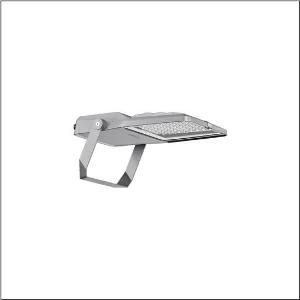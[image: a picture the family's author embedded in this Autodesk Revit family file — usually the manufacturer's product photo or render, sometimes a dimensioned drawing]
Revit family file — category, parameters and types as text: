
# Revit family: floodlight_fl_21_mini___pl64_5xa7776c2e1a_42f0
name_source: partatom
category: Lighting Fixtures
units: mm (PartAtom-declared; Revit-internal decimal feet)

## family parameters
Cut with Voids When Loaded = No
Host = Face
Light Source = No
Part Type = Normal
Room Calculation Point = No
Round Connector Dimension = Use Diameter
Shared = No

## types (1)
- --- (1 x LED, 11770 lm, 89 W, 3000K)
    Apparent Load = 89 VA
    CIE Flux Codes = 28 80 98 100 100
    Color Rendering = 70
    Color Temperature = 3000K
    Default Elevation = 1800 mm
    Description = Floodlight FL 21 mini, floodlight, primary light control with lens, of PMMA, primary optical cover: protective disc, of toughened safety glass, transparent, light distribution: PL64, light emission: direct distribution, installation type: surface-mounted, LED, High Power LED, rated luminous flux: 11.770lm, luminous efficacy: 132lm/W, light colour: 730, colour temperature: 3000K, control gear: Smart Interface (Zhaga), control: flexible luminous flux parameterisation, time-dependent luminous flux control, constant luminous flux control, overheat protection, pre-setting: logarithmic dimming characteristic, with terminal, 6-pole, mains connection: 220..240V, AC, 50/60Hz, start of lifetime: 89W, end of service life: 94W, reduction: 43W, luminaire housing, of diecast aluminium, powder-coated, SITECO metallic grey (DB 702S), corrosivity category C5 mid according to DIN EN ISO 12944, suitable for swimming pools, chlorine-resistant, sealing non-destructively replaceable, mounting bracket, of steel, galvanised, powder-coated, SITECO metallic grey (DB 702S), Smart Interface below and above, protection rating (complete): IP66, insulation class (complete): insulation class II (safety insulation), certification: CE, ENEC, VDE, protection symbol: D, impact resistance: IK08, permissible operating ambient temperature: -40..+40°C, permissible operating ambient temperature for outdoor applications: -40..+50°C, standard: DIN EN 12944, LABS conformity tested according to VDMA 24364:2018-05, packaging unit: 1 piece

Light Distribution: PL64
    Height = 70 mm
    Lamp = 1 x LED
    Lamp Light Flux = 11770 lm
    Lamp Power = 89 W
    Lamp count = 1
    Length = 485 mm
    Luminous efficacy = 132 lm/W
    Manufacturer = Siteco
    ModVariant = No
    Model = 5XA7776C2E1A
    Mounting Place = Pole
    Mounting Type = Pole annexe
    Number of Poles = 1
    OnlyDefault = Yes
    Power Factor = 1
    Product Name = Floodlight FL 21 mini | PL64
    Product group = floodlight | pylon annexe
    ProductGroupID = 6201
    Protection Class = Protection class II
    Protection Degree = IP 66
    RLX_Detail_Level = 1
    RLX_Emergency_Light_Flux = 0 lm
    RLX_Emergency_Type = 0
    RLX_Emergency_Type_DB = No
    RlxData = <blob elided: 95997 chars, md5=2740ca23>
    Socket = socket
    Standby Power = 0 W
    System Light Flux = 11770 lm
    System Power = 89 W
    Type Comments = factory setting: luminous flux: 100 % | dim-lin: 254 | 456 mA
    Type Image = l_1006845.jpg
    URL = http://relux.com
    VarID = @adj_166407
    Voltage = 0 V
    Weight = 0.00 kg
    Width = 337 mm

## geometry (parser evidence)
native form markers: Blend x4, Sweep x13
no freeform markers — native parametric forms only
